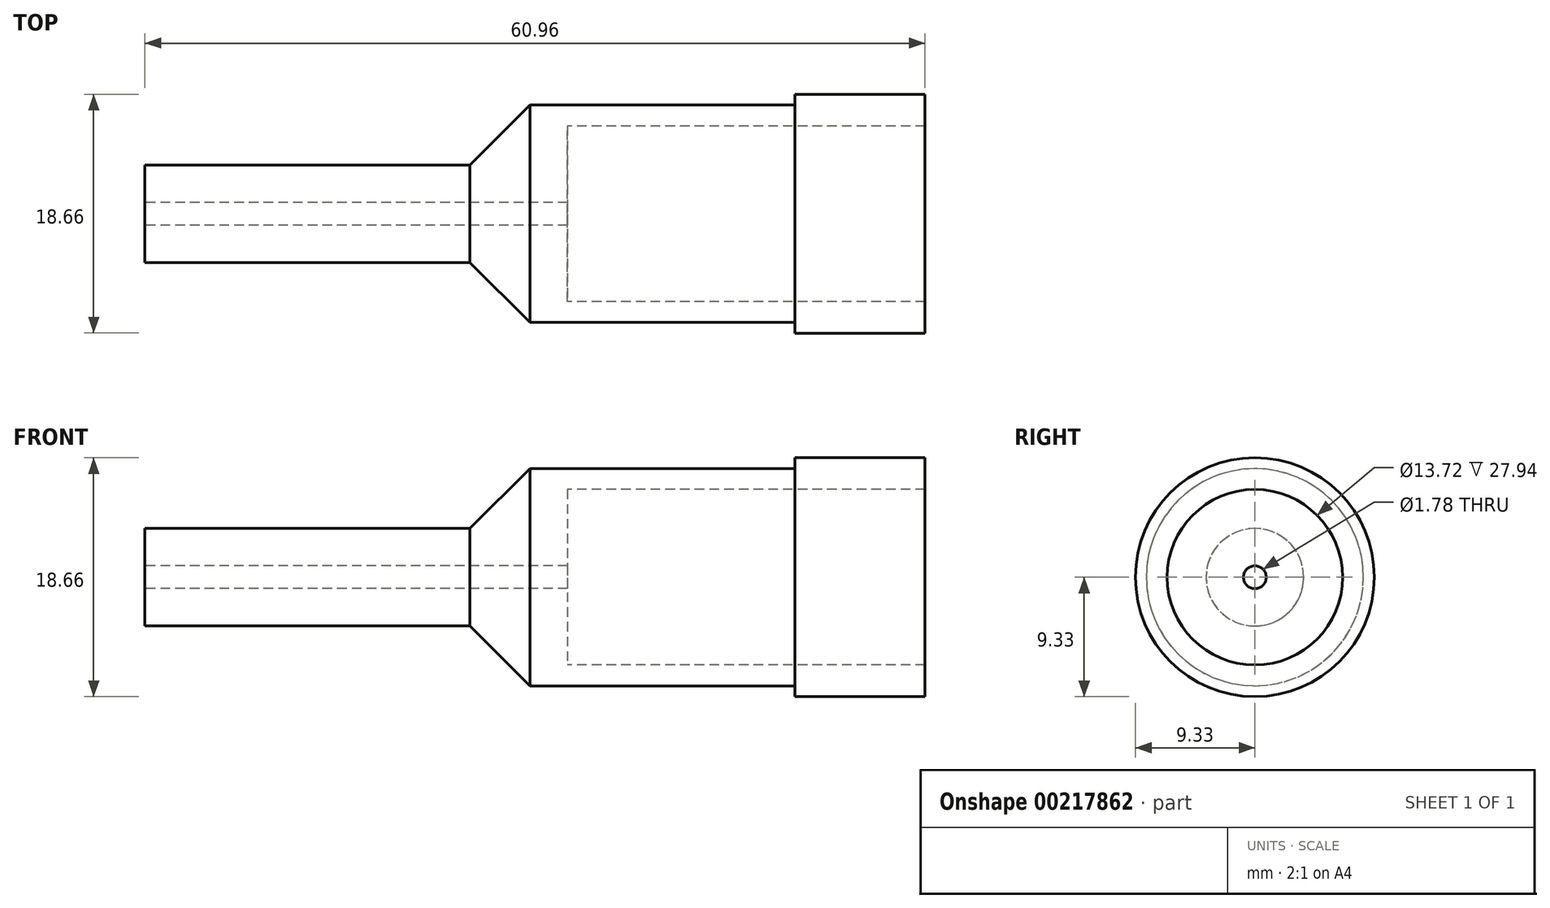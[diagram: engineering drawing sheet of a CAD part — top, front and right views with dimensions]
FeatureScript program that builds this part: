
annotation { "Feature Type Name" : "Feature", "Feature Type Description" : "" }
export const myFeature = defineFeature(function(context is Context, id is Id, definition is map)
    precondition{}
    {
        {
            var Q0;
            Q0=qCreatedBy(makeId("Front.planeOp"),FACE);
            var sketch = newSketch(context, id + "F0", { "sketchPlane" : qUnion([Q0])});
            skLineSegment(sketch, "E0", {"start": v(-2.54, 0) * mm, "end": v(-33.02, 0) * mm});
            skLineSegment(sketch, "E1", {"start": v(-38.66, 3.8) * mm, "end": v(27.89, 3.8) * mm, "construction": true});
            skLineSegment(sketch, "E2", {"start": v(27.94, -5.52) * mm, "end": v(27.94, 3.8) * mm});
            skLineSegment(sketch, "E3", {"start": v(27.94, -5.52) * mm, "end": v(17.78, -5.52) * mm});
            skLineSegment(sketch, "E4", {"start": v(17.78, -5.52) * mm, "end": v(17.78, -4.67) * mm});
            skLineSegment(sketch, "E5", {"start": v(17.78, -4.67) * mm, "end": v(-2.54, -4.67) * mm});
            skLineSegment(sketch, "E6", {"start": v(-2.54, -4.67) * mm, "end": v(-2.54, 0) * mm});
            skLineSegment(sketch, "E7", {"start": v(-33.02, 2.92) * mm, "end": v(0, 2.92) * mm});
            skLineSegment(sketch, "E8", {"start": v(0, -3.05) * mm, "end": v(27.94, -3.05) * mm});
            skLineSegment(sketch, "E9", {"start": v(0, 2.92) * mm, "end": v(0, -3.05) * mm});
            skLineSegment(sketch, "E10", {"start": v(-33.02, 2.92) * mm, "end": v(-33.02, 0) * mm});
            skPoint(sketch, "E11.orphan", {"position": v(-33.02, 3.8) * mm});
            skSolve(sketch);
        }
        {
            var Q0;
            Q0 = qSketchRegion(id + "F0", true);
            var Q1;
            Q1=sQuery(id+"F0.wireOp",EDGE,"E1");
            revolve(context, id + "F1", {"entities" : qUnion([Q0]), "axis" : qUnion([Q1]), "revolveType" : RevolveType.FULL});
        }
        {
            var Q0;
            Q0=makeQuery(id+"F1.opRevolve","SWEPT_EDGE",EDGE,{"disambiguationData":[OSD([sQuery(id+"F0.wireOp",EDGE,"E0"),sQuery(id+"F0.wireOp",EDGE,"E6")])]});
            chamfer(context, id + "F2", {"entities" : qUnion([Q0]), "width" : 5.08 * mm, "tangentPropagation" : true});
        }
    });
